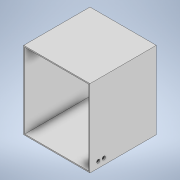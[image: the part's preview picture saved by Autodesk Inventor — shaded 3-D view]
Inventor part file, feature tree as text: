
AUTODESK INVENTOR PART (.ipt)
format: ipt  version: 2020 (Build 240168000, 168)  size: 124,928 bytes
history: native  units: mm
features: extrude x3, sketch x3, shell x1
ambient origin geometry x8: Origin, YZ Plane, XZ Plane, XY Plane, X Axis, Y Axis, Z Axis, Center Point
bodies: Solid1 (feature_tree)
feature tree (7):
  extrude  "Base"  Depth=350.0mm
  shell  "Shell1"  Thickness=300.0mm
  extrude  "Wire holes"  Depth=5.0mm
  extrude  "Exhaust"  Depth=350.0mm
  sketch  "Sketch2"  dims[d0=300.0mm d1=350.0mm d2=300.0mm d3=0.0mm]
  sketch  "Sketch3"  dims[d4=5.0mm d5=15.0mm]
  sketch  "Sketch4"  dims[d9=37.5mm d10=27.5mm d11=20.0mm d13=25.0mm d14=10.0mm d16=10.0mm d18=350.0mm d19=0.0mm d20=50.0mm d21=75.0mm d22=45.0deg d23=350.0mm d24=0.0mm]
